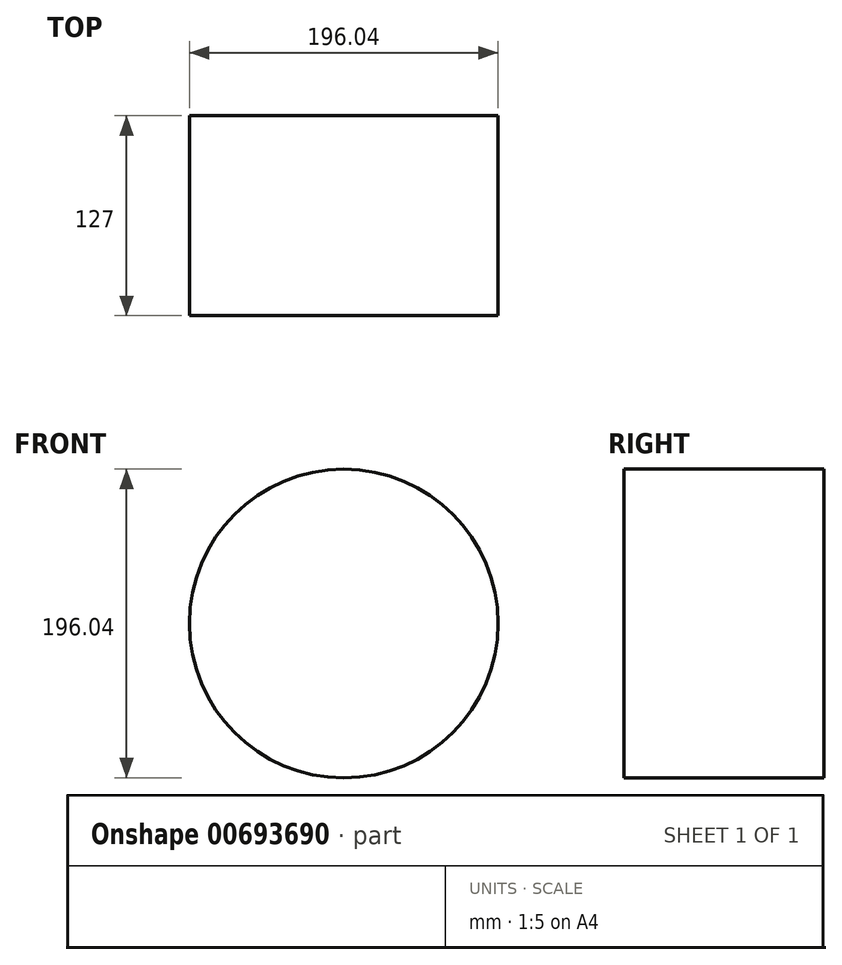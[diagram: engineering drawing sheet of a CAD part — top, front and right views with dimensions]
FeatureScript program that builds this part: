
annotation { "Feature Type Name" : "Feature", "Feature Type Description" : "" }
export const myFeature = defineFeature(function(context is Context, id is Id, definition is map)
    precondition{}
    {
        {
            var Q0;
            Q0=qCreatedBy(makeId("Front.planeOp"),FACE);
            var sketch = newSketch(context, id + "F0", { "sketchPlane" : qUnion([Q0])});
            skCircle(sketch, "E0", {"center": v(0, 0) * mm, "radius": 98.02 * mm});
            skSolve(sketch);
        }
        {
            var Q0;
            Q0 = qSketchRegion(id + "F0", true);
            extrude(context, id + "F1", {"entities" : qUnion([Q0]), "depth" : 127 * mm, "offsetDistance" : 25.4 * mm});
        }
    });
